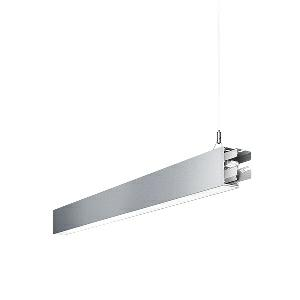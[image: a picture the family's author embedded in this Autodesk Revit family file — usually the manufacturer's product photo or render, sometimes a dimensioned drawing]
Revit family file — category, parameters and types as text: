
# Revit family: idoo_line_-_ilp_4000_830_d_mid_00805741_bc03
name_source: partatom
category: Lighting Fixtures
units: mm (PartAtom-declared; Revit-internal decimal feet)

## family parameters
Cut with Voids When Loaded = No
Host = Face
Light Source = No
Part Type = Normal
Room Calculation Point = No
Round Connector Dimension = Use Diameter
Shared = No

## types (1)
- IDOO.line - ILP 4000/830/D MID (1 x LED, 3750 lm, 3000K)
    Apparent Load = 29 VA
    Approval mark = CE
    CIE Flux Codes = 66 91 98 40 100
    Color Rendering = 80-89
    Color Temperature = 3000K
    Control Gear = Electronic ballast
    Default Elevation = 1800 mm
    Description = ILP 4000/830/D|Suspended luminaire|light source: LED|connected load: 220-240 V, 50/60 Hz|Power consumption: approx. 29 W|standby: approx. 0,15|luminous flux: 3750 lm|luminous efficacy: 129 lm/W|light distribution: Direct/indirect|direct ratio: approx. 40 %|colour temperature: Warm white, ca. 3000 K|color rendering index (CRI): >= 80|chromaticity tolerance:  3 SDCM|System of protection: IP 40|technology: Continuously dimmable|luminaire body|material: Sectional aluminium|colour: Silver|lamp cover: Acrylic (PMMA), Clear|mains lead: 1,0 m With free stranded wires|Fastening: Steel cable 0.3 - 0.7 m|glare control: Prism aperture|luminance(L65): <= 2700 cd/m|unified glare rating(4H 8H): <=  16|special features: DALI Load 1x, TouchDIM - dimming via standard switch, Through-wired, up to 18 m on one mains connection, Flicker-free, Suitable as emergency lighting, Mechanical and electrical connection of the individual modules without tools|
    Frequency = 50 Hz
    Height = 110 mm
    Lamp = 1 x LED
    Lamp Light Flux = 3750 lm
    Lamp count = 1
    Length = 1402 mm
    Luminous efficacy = 129 lm/W
    Manufacturer = Waldmann
    ModVariant = No
    Model = 00805741
    Mounting Place = Ceiling
    Mounting Type = Pendant
    Number of Poles = 1
    OnlyDefault = Yes
    Power Factor = 1
    Product Name = IDOO.line - ILP 4000/830/D MID
    Product group = Suspended luminaire
    ProductGroupID = 9
    Protection Class = Protection class I
    Protection Degree = IP 40
    RLX_Detail_Level = 1
    RLX_Emergency_Light_Flux = 0 lm
    RLX_Emergency_Type = 0
    RLX_Emergency_Type_DB = No
    RlxData = <blob elided: 21773 chars, md5=c4347fee>
    Socket = socket
    Standby Power = 0 W
    System Light Flux = 3750 lm
    System Power = 29 W
    Type Comments = Product without accessories
    Type Image = 113311000-00692597.jpg
    URL = http://relux.com
    VarID = ---
    Voltage = 230 V
    Voltage Range = 220-240 V
    Weight = 0.00 kg
    Width = 60 mm  [stored 0.19685 ft]

note: [stored X ft] marks values corroborated as IEEE doubles in the binary element streams (Revit-internal decimal feet)

## geometry (parser evidence)
native form markers: Blend x4, Sweep x14
no freeform markers — native parametric forms only
